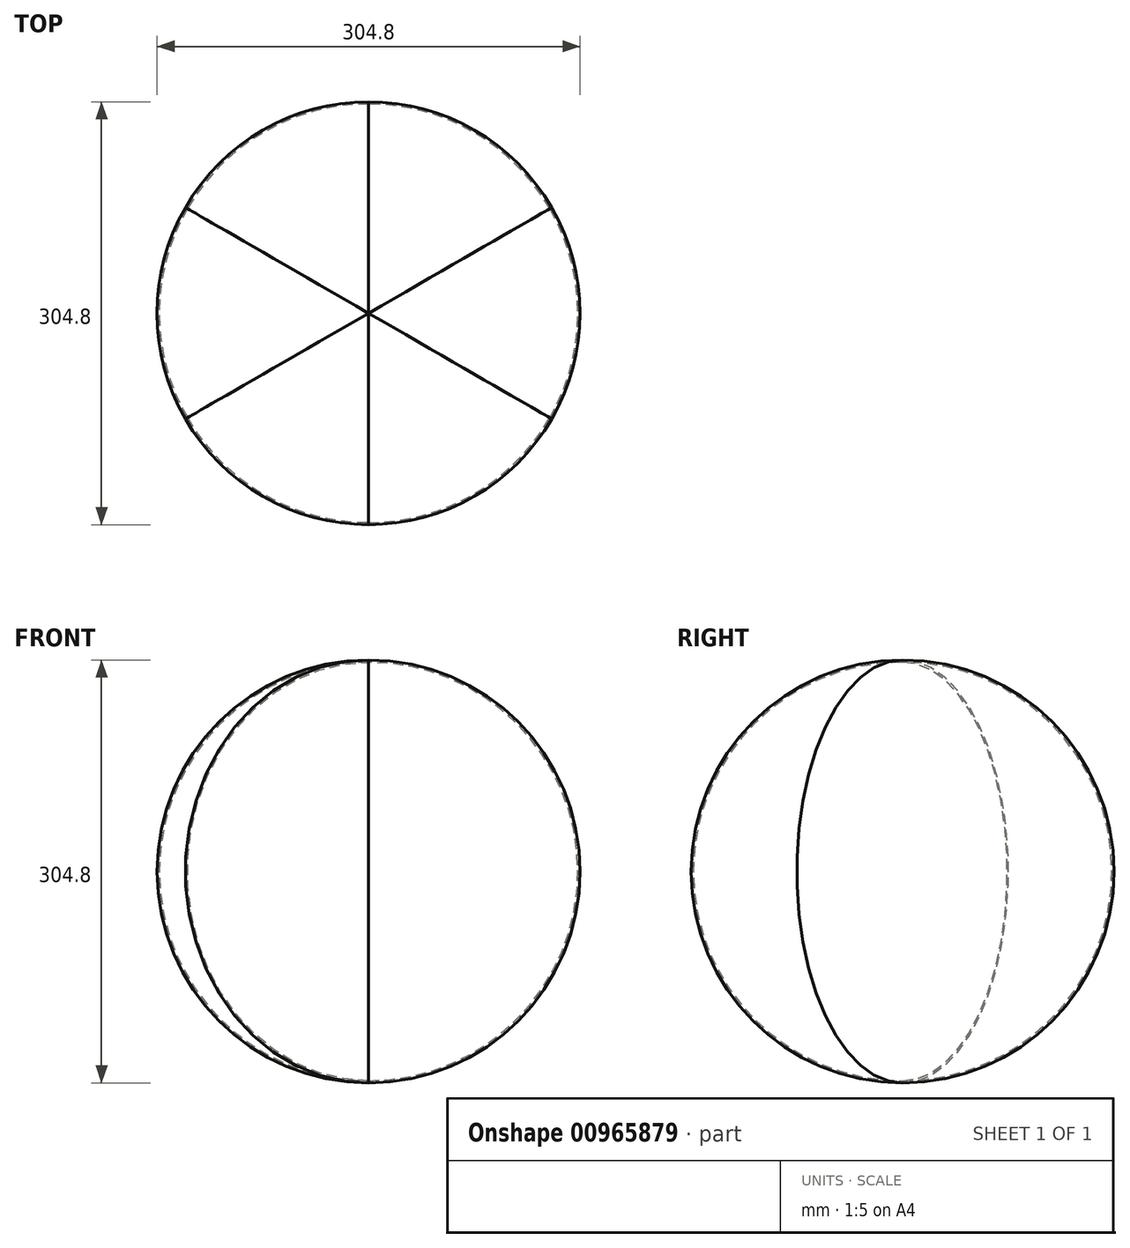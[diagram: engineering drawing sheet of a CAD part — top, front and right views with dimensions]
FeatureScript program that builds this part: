
annotation { "Feature Type Name" : "Feature", "Feature Type Description" : "" }
export const myFeature = defineFeature(function(context is Context, id is Id, definition is map)
    precondition{}
    {
        {
            var Q0;
            Q0=qCreatedBy(makeId("Front.planeOp"),FACE);
            var sketch = newSketch(context, id + "F0", { "sketchPlane" : qUnion([Q0])});
            skArc(sketch, "E0", {"start": v(0, -152.4) * mm, "mid": v(152.4, 0) * mm, "end": v(0, 152.4) * mm});
            skArc(sketch, "E1", {"start": v(0, -150.81) * mm, "mid": v(150.81, 0) * mm, "end": v(0, 150.81) * mm});
            skLineSegment(sketch, "E2", {"start": v(0, 152.4) * mm, "end": v(0, -152.4) * mm});
            skSolve(sketch);
        }
        {
            var Q0;
            {var subQ0=sQuery(id+"F0.wireOp",EDGE,"E0");Q0=makeQuery(id+"F0.imprint","IMPRINT",FACE,{"disambiguationData":[TD([[makeQuery(id+"F0.imprint","IMPRINT",EDGE,{"derivedFrom":subQ0}),1.0]])]});}
            var Q1;
            Q1=sQuery(id+"F0.wireOp",EDGE,"E2");
            revolve(context, id + "F1", {"surfaceOperationType" : NewSurfaceOperationType.NEW, "entities" : qUnion([Q0]), "axis" : qUnion([Q1]), "revolveType" : RevolveType.SYMMETRIC, "angle" : 60 * degree});
        }
        {
            var Q0;
            Q0=qCreatedBy(makeId("Front.planeOp"),FACE);
            var sketch = newSketch(context, id + "F2", { "sketchPlane" : qUnion([Q0])});
            skLineSegment(sketch, "E3", {"start": v(0, 152.55) * mm, "end": v(0, -151.84) * mm});
            skSolve(sketch);
        }
        {
            var Q0;
            Q0=makeQuery(id+"F1.opRevolve","SWEPT_BODY",BODY,{"disambiguationData":[OSD([sQuery(id+"F0.wireOp",EDGE,"E0"),sQuery(id+"F0.wireOp",EDGE,"E1"),sQuery(id+"F0.wireOp",EDGE,"E2")])]});
            var Q1;
            Q1=sQuery(id+"F2.wireOp",EDGE,"E3");
            circularPattern(context, id + "F3", {"entities" : qUnion([Q0]), "axis" : qUnion([Q1]), "angle" : 360 * degree, "instanceCount" : 6, "equalSpace" : true});
        }
    });
